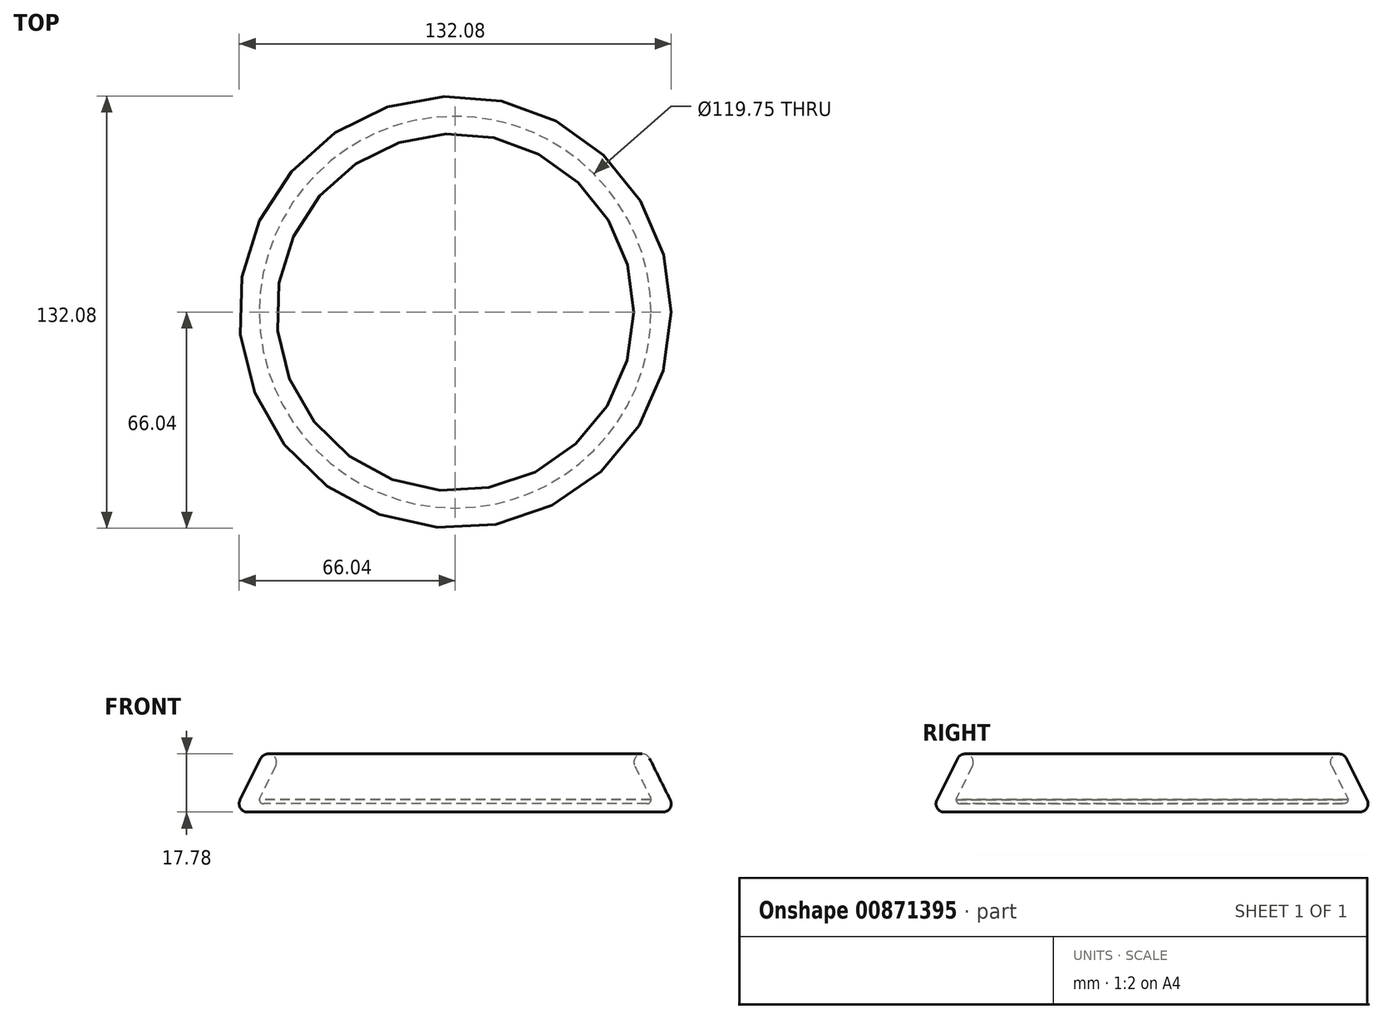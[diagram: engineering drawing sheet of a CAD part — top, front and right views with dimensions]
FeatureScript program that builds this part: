
annotation { "Feature Type Name" : "Feature", "Feature Type Description" : "" }
export const myFeature = defineFeature(function(context is Context, id is Id, definition is map)
    precondition{}
    {
        {
            var Q0;
            Q0=qCreatedBy(makeId("Top.planeOp"),FACE);
            var sketch = newSketch(context, id + "F0", { "sketchPlane" : qUnion([Q0])});
            skCircle(sketch, "E0", {"center": v(0, 0) * mm, "radius": 63.5 * mm});
            skSolve(sketch);
        }
        {
            var Q0;
            Q0=qCreatedBy(makeId("Top.planeOp"),FACE);
            cPlane(context, id + "F1", {"entities" : qUnion([Q0]), "cplaneType" : CPlaneType.OFFSET, "offset" : 12.7 * mm, "width" : 152.4 * mm, "height" : 152.4 * mm});
        }
        {
            var Q0;
            Q0=qCreatedBy(id+"F1.planeOp",FACE);
            var sketch = newSketch(context, id + "F2", { "sketchPlane" : qUnion([Q0])});
            skCircle(sketch, "E1", {"center": v(0, 0) * mm, "radius": 57.15 * mm});
            skSolve(sketch);
        }
        {
            var Q0;
            Q0=qCreatedBy(makeId("Front.planeOp"),FACE);
            var sketch = newSketch(context, id + "F3", { "sketchPlane" : qUnion([Q0])});
            skLineSegment(sketch, "E2.0", {"start": v(-57.15, 12.7) * mm, "end": v(57.15, 12.7) * mm, "construction": true});
            skLineSegment(sketch, "E3.0", {"start": v(-63.5, 0) * mm, "end": v(58.6, 0) * mm, "construction": true});
            skArc(sketch, "E4", {"start": v(59.42, 13.84) * mm, "mid": v(56.01, 14.97) * mm, "end": v(54.88, 11.56) * mm});
            skArc(sketch, "E5", {"start": v(63.5, -2.54) * mm, "mid": v(65.66, -1.34) * mm, "end": v(65.77, 1.14) * mm});
            skLineSegment(sketch, "E6", {"start": v(59.42, 13.84) * mm, "end": v(65.77, 1.14) * mm});
            skLineSegment(sketch, "E7", {"start": v(54.88, 11.56) * mm, "end": v(59.74, 1.84) * mm});
            skLineSegment(sketch, "E8", {"start": v(0, 0) * mm, "end": v(0, -2.54) * mm});
            skLineSegment(sketch, "E9", {"start": v(0, -2.54) * mm, "end": v(63.5, -2.54) * mm});
            skLineSegment(sketch, "E10", {"start": v(0, 0) * mm, "end": v(60.66, 0) * mm});
            skPoint(sketch, "E11.visualSharp", {"position": v(60.66, 0) * mm});
            skArc(sketch, "E11.filletArc", {"start": v(58.6, 0) * mm, "mid": v(59.69, 0.6) * mm, "end": v(59.74, 1.84) * mm});
            skLineSegment(sketch, "E12", {"start": v(59.87, 1.35) * mm, "end": v(59.87, -2.54) * mm});
            skSolve(sketch);
        }
        {
            var Q0;
            Q0 = qSketchRegion(id + "F3", true);
            var Q1;
            Q1=sQuery(id+"F3.wireOp",EDGE,"E8");
            revolve(context, id + "F4", {"surfaceOperationType" : NewSurfaceOperationType.NEW, "entities" : qUnion([Q0]), "axis" : qUnion([Q1]), "revolveType" : RevolveType.FULL});
        }
    });
